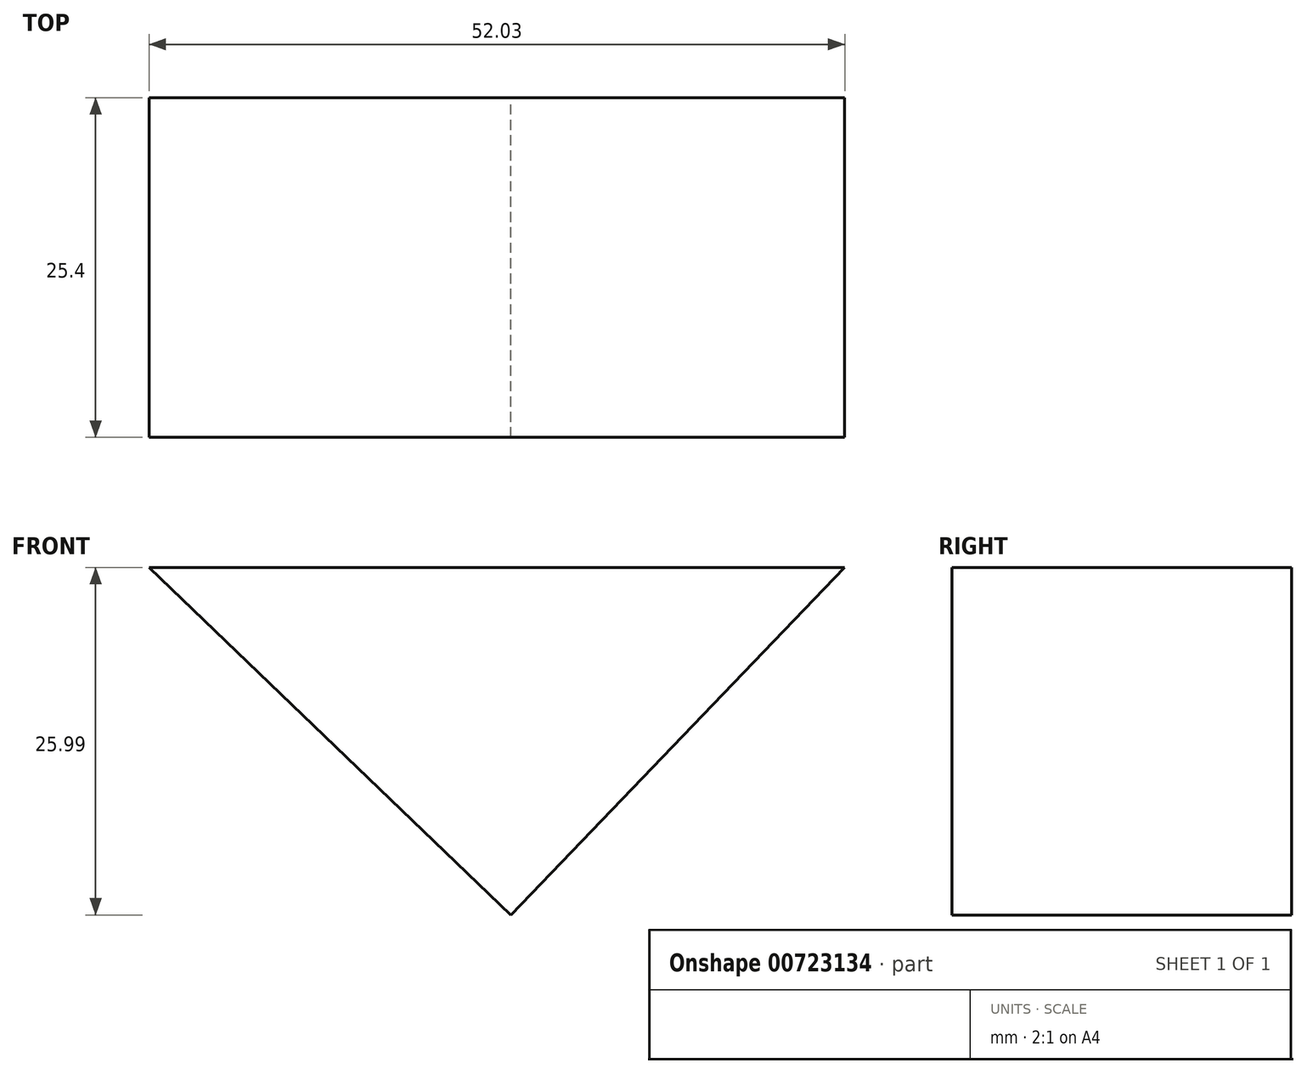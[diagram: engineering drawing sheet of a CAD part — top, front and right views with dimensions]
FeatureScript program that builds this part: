
annotation { "Feature Type Name" : "Feature", "Feature Type Description" : "" }
export const myFeature = defineFeature(function(context is Context, id is Id, definition is map)
    precondition{}
    {
        {
            var Q0;
            Q0=qCreatedBy(makeId("Front.planeOp"),FACE);
            var sketch = newSketch(context, id + "F0", { "sketchPlane" : qUnion([Q0])});
            skLineSegment(sketch, "E0", {"start": v(-54.08, 51.98) * mm, "end": v(0, 0) * mm});
            skLineSegment(sketch, "E1", {"start": v(0, 0) * mm, "end": v(48.14, 50.08) * mm});
            skLineSegment(sketch, "E2", {"start": v(48.14, 50.08) * mm, "end": v(-54.08, 51.98) * mm});
            skPoint(sketch, "E3.firstSnap0", {"position": v(-27.04, 26) * mm});
            skPoint(sketch, "E3.oppositeSnap0", {"position": v(-27.04, 26) * mm});
            skLineSegment(sketch, "E3.bottom", {"start": v(47.67, 26) * mm, "end": v(-27.04, 26) * mm});
            skLineSegment(sketch, "E3.top", {"start": v(47.67, 0) * mm, "end": v(-27.04, 0) * mm});
            skLineSegment(sketch, "E3.left", {"start": v(47.67, 26) * mm, "end": v(47.67, 0) * mm});
            skLineSegment(sketch, "E3.right", {"start": v(-27.04, 26) * mm, "end": v(-27.04, 0) * mm});
            skSolve(sketch);
        }
        {
            var Q0;
            {var subQ0=sQuery(id+"F0.wireOp",EDGE,"E1");var subQ3=sQuery(id+"F0.wireOp",EDGE,"E3.bottom");var subQ5=makeQuery(id+"F0.imprint","INTERSECT",VERTEX,{"derivedFrom":[subQ0,subQ3]});Q0=makeQuery(id+"F0.imprint","IMPRINT",FACE,{"disambiguationData":[TD([[makeQuery(id+"F0.imprint","IMPRINT",EDGE,{"disambiguationData":[TD([[subQ5,1.0]])],"derivedFrom":subQ0}),1.0]])]});}
            extrude(context, id + "F1", {"entities" : qUnion([Q0]), "depth" : 25.4 * mm, "offsetDistance" : 25.4 * mm});
        }
    });
